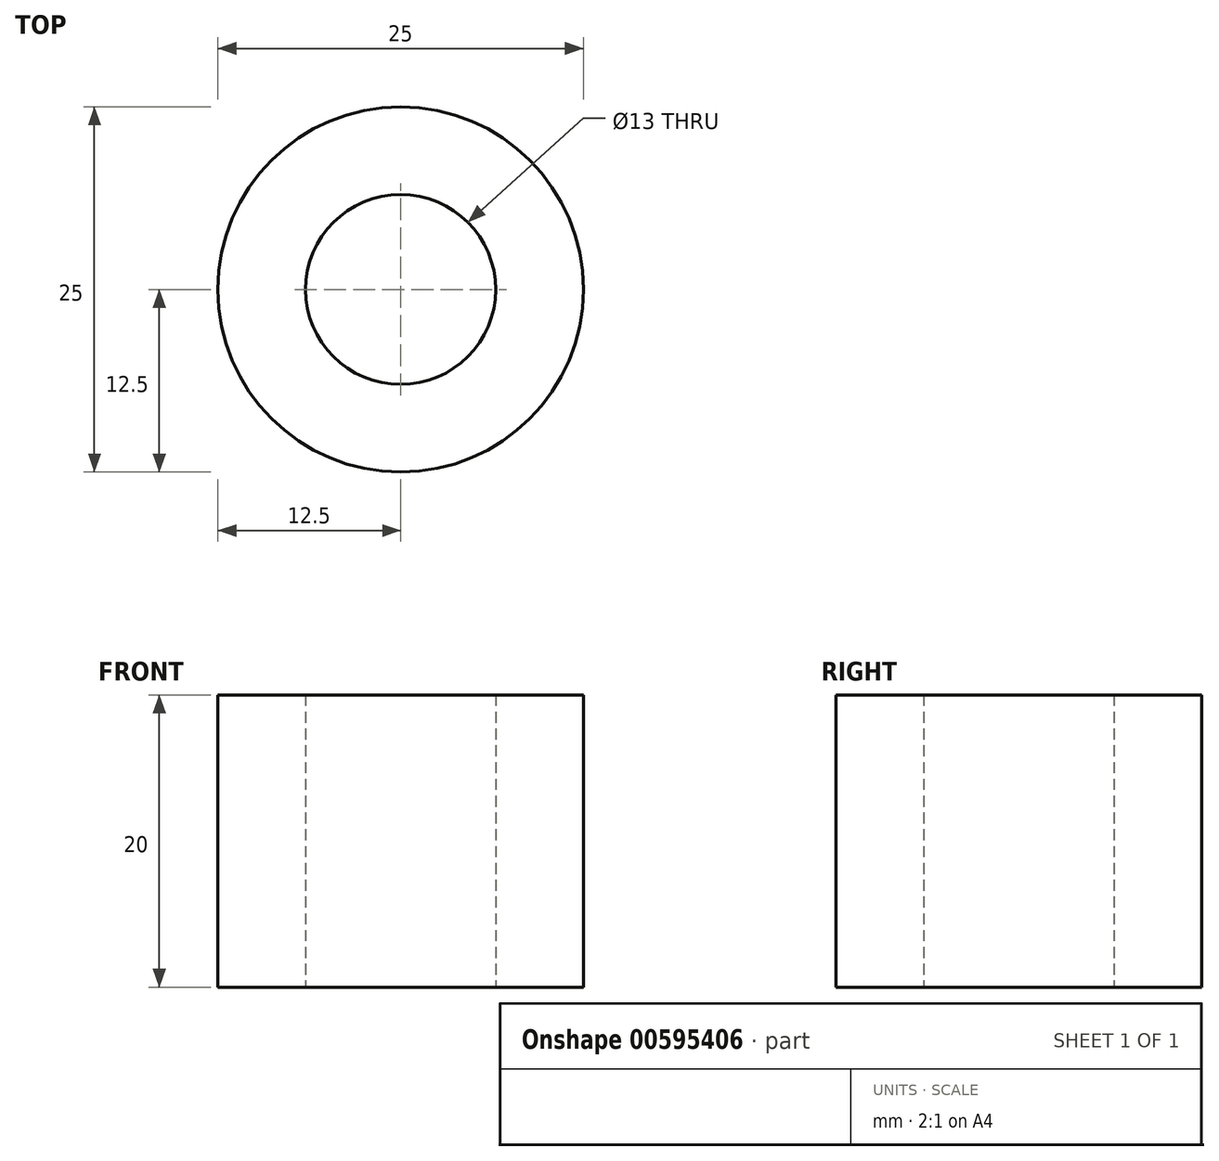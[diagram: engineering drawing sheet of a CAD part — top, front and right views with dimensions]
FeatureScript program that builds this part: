
annotation { "Feature Type Name" : "Feature", "Feature Type Description" : "" }
export const myFeature = defineFeature(function(context is Context, id is Id, definition is map)
    precondition{}
    {
        {
            var Q0;
            Q0=qCreatedBy(makeId("Top.planeOp"),FACE);
            var sketch = newSketch(context, id + "F0", { "sketchPlane" : qUnion([Q0])});
            skCircle(sketch, "E0", {"center": v(0, 0) * mm, "radius": 12.5 * mm});
            skCircle(sketch, "E1", {"center": v(0, 0) * mm, "radius": 6.5 * mm});
            skSolve(sketch);
        }
        {
            var Q0;
            Q0 = qSketchRegion(id + "F0", true);
            extrude(context, id + "F1", {"entities" : qUnion([Q0]), "depth" : 20 * mm, "offsetDistance" : 25 * mm});
        }
    });
